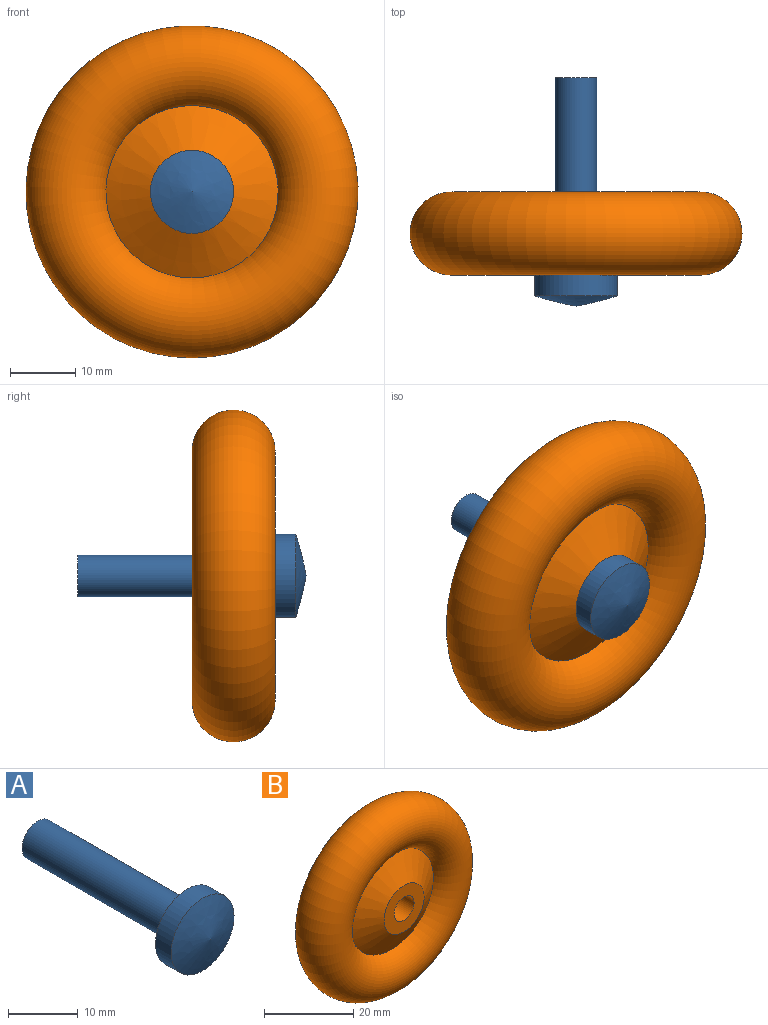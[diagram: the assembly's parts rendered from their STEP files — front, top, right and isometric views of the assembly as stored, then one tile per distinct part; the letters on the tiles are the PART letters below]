
ASSEMBLY  parts=2 mates=1
PART A: 5 faces, bbox 12.7x33.3x12.7 mm
  f0: plane 6.35x6.35mm, normal (0,1,0), area 31.7mm2, adj f1
  f1: cylinder r=3.17mm len=30.16mm, axis (0,-1,0), area 601.7mm2, adj f0,f2
  f2: plane 12.7x12.7mm, normal (0,1,0), area 95mm2, adj f1,f3
  f3: cylinder r=6.35mm len=12.7mm, axis (0,-1,0), area 126.7mm2, adj f2,f4
  f4: revolved ~12.7x6.35mm, area 0mm2, adj f3
PART B: 5 faces, bbox 55x12.7x55 mm
  f0: plane 12.7x12.7mm, normal (0,-1,0), area 95mm2, adj f1,f4
  f1: cylinder r=3.17mm len=12.7mm, axis (0,-1,0), area 253.4mm2, adj f0,f2
  f2: plane 38.1x38.1mm, normal (0,1,0), area 1108.4mm2, adj f1,f3
  f3: torus R=19.05mm, axis (0,-1,0), area 3635.4mm2, adj f2,f4
  f4: cone r=6.35mm half-angle=60deg, axis (0,1,0), area 483.4mm2, adj f0,f3
PLACE A t=(-11.52,-19.24,-9.37)mm
PLACE B t=(-11.52,-19.24,-9.37)mm
MATE revolute B.f1 <-> A.f1  axis (0,-1,0) through (-11.52,-25.59,-9.37)mm
